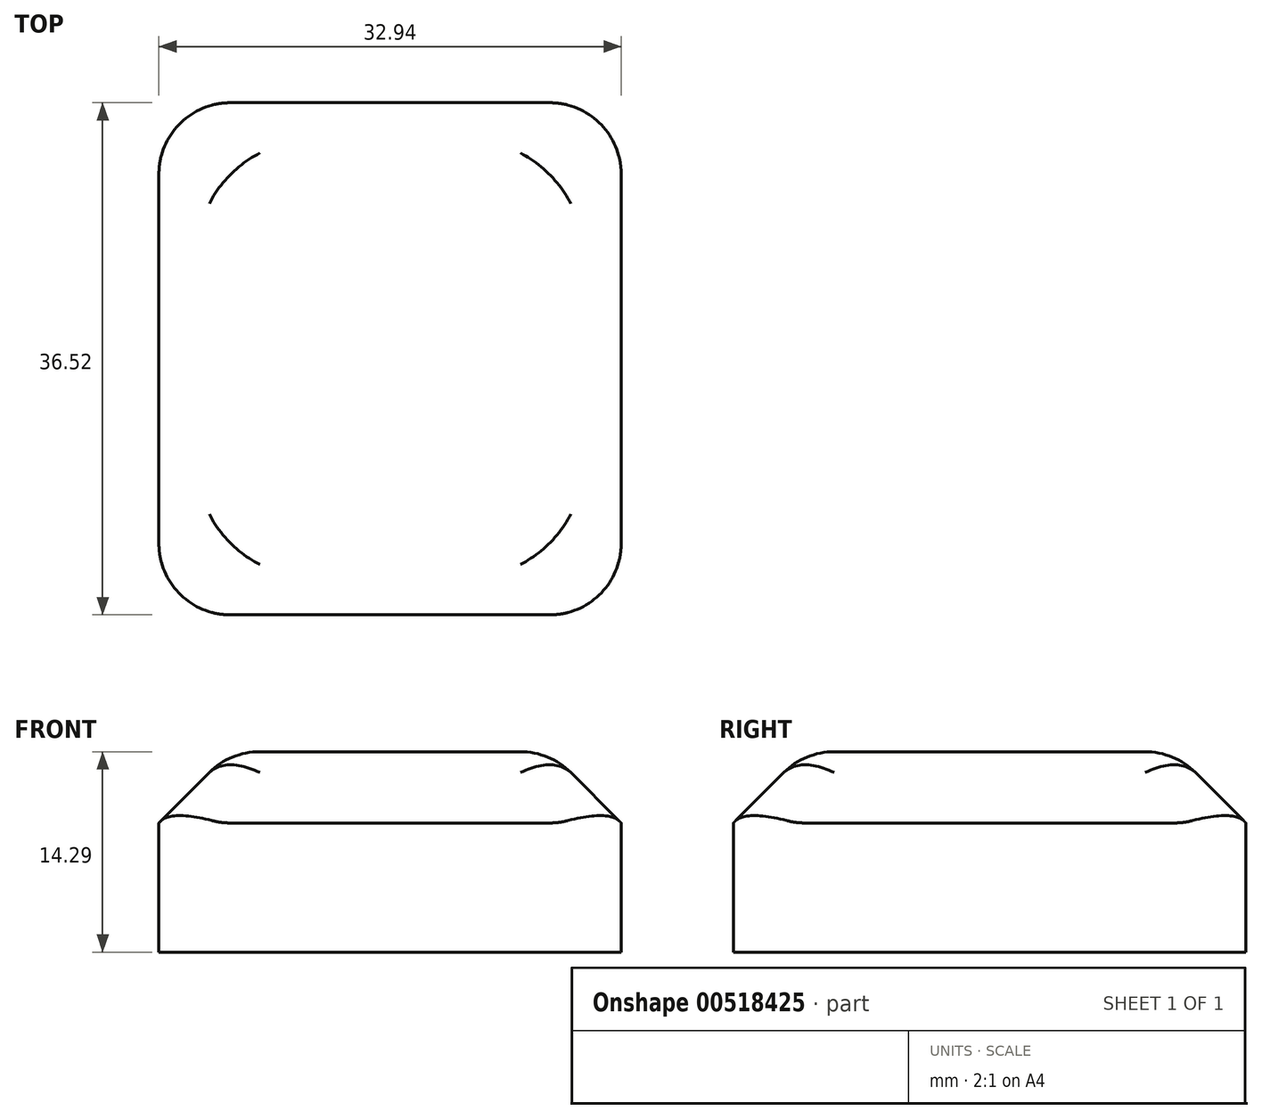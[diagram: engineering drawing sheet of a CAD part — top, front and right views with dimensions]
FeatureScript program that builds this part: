
annotation { "Feature Type Name" : "Feature", "Feature Type Description" : "" }
export const myFeature = defineFeature(function(context is Context, id is Id, definition is map)
    precondition{}
    {
        {
            var Q0;
            Q0=qCreatedBy(makeId("Top.planeOp"),FACE);
            var sketch = newSketch(context, id + "F0", { "sketchPlane" : qUnion([Q0])});
            skLineSegment(sketch, "E0.bottom", {"start": v(16.47, -18.26) * mm, "end": v(-16.47, -18.26) * mm});
            skLineSegment(sketch, "E0.top", {"start": v(16.47, 18.26) * mm, "end": v(-16.47, 18.26) * mm});
            skLineSegment(sketch, "E0.left", {"start": v(16.47, -18.26) * mm, "end": v(16.47, 18.26) * mm});
            skLineSegment(sketch, "E0.right", {"start": v(-16.47, -18.26) * mm, "end": v(-16.47, 18.26) * mm});
            skPoint(sketch, "E0.middle", {"position": v(0, 0) * mm});
            skSolve(sketch);
        }
        {
            var Q0;
            Q0 = qSketchRegion(id + "F0", true);
            extrude(context, id + "F1", {"entities" : qUnion([Q0]), "depth" : 14.29 * mm, "offsetDistance" : 25.4 * mm});
        }
        {
            var Q0;
            Q0=makeQuery(id+"F1.opExtrude","CAP_FACE",FACE,{"disambiguationData":[OSD([sQuery(id+"F0.wireOp",EDGE,"E0.bottom"),sQuery(id+"F0.wireOp",EDGE,"E0.top"),sQuery(id+"F0.wireOp",EDGE,"E0.left"),sQuery(id+"F0.wireOp",EDGE,"E0.right")])],"isStart":false});
            chamfer(context, id + "F2", {"entities" : qUnion([Q0]), "width" : 5.08 * mm, "tangentPropagation" : true});
        }
        {
            var Q0;
            Q0=makeQuery(id+"F1.opExtrude","SWEPT_EDGE",EDGE,{"disambiguationData":[OSD([sQuery(id+"F0.wireOp",EDGE,"E0.bottom"),sQuery(id+"F0.wireOp",EDGE,"E0.left")])]});
            var Q1;
            Q1=makeQuery(id+"F1.opExtrude","SWEPT_EDGE",EDGE,{"disambiguationData":[OSD([sQuery(id+"F0.wireOp",EDGE,"E0.top"),sQuery(id+"F0.wireOp",EDGE,"E0.left")])]});
            var Q2;
            Q2=makeQuery(id+"F1.opExtrude","SWEPT_EDGE",EDGE,{"disambiguationData":[OSD([sQuery(id+"F0.wireOp",EDGE,"E0.top"),sQuery(id+"F0.wireOp",EDGE,"E0.right")])]});
            var Q3;
            Q3=makeQuery(id+"F1.opExtrude","SWEPT_EDGE",EDGE,{"disambiguationData":[OSD([sQuery(id+"F0.wireOp",EDGE,"E0.bottom"),sQuery(id+"F0.wireOp",EDGE,"E0.right")])]});
            var Q4;
            Q4=makeQuery(id+"F1.opExtrude","CAP_FACE",FACE,{"disambiguationData":[OSD([sQuery(id+"F0.wireOp",EDGE,"E0.bottom"),sQuery(id+"F0.wireOp",EDGE,"E0.top"),sQuery(id+"F0.wireOp",EDGE,"E0.left"),sQuery(id+"F0.wireOp",EDGE,"E0.right")])],"isStart":false});
            var Q5;
            Q5=makeQuery(id+"F2.opChamfer","BLEND_EDGE",EDGE,{"blendedFrom":[makeQuery(id+"F1.opExtrude","CAP_EDGE",EDGE,{"disambiguationData":[OSD([sQuery(id+"F0.wireOp",EDGE,"E0.bottom")])],"isStart":false}),makeQuery(id+"F1.opExtrude","CAP_EDGE",EDGE,{"disambiguationData":[OSD([sQuery(id+"F0.wireOp",EDGE,"E0.right")])],"isStart":false})],"blendedInto":[]});
            var Q6;
            Q6=makeQuery(id+"F2.opChamfer","BLEND_EDGE",EDGE,{"blendedFrom":[makeQuery(id+"F1.opExtrude","CAP_EDGE",EDGE,{"disambiguationData":[OSD([sQuery(id+"F0.wireOp",EDGE,"E0.bottom")])],"isStart":false}),makeQuery(id+"F1.opExtrude","CAP_EDGE",EDGE,{"disambiguationData":[OSD([sQuery(id+"F0.wireOp",EDGE,"E0.left")])],"isStart":false})],"blendedInto":[]});
            var Q7;
            Q7=makeQuery(id+"F2.opChamfer","BLEND_EDGE",EDGE,{"blendedFrom":[makeQuery(id+"F1.opExtrude","CAP_EDGE",EDGE,{"disambiguationData":[OSD([sQuery(id+"F0.wireOp",EDGE,"E0.top")])],"isStart":false}),makeQuery(id+"F1.opExtrude","CAP_EDGE",EDGE,{"disambiguationData":[OSD([sQuery(id+"F0.wireOp",EDGE,"E0.left")])],"isStart":false})],"blendedInto":[]});
            var Q8;
            Q8=makeQuery(id+"F2.opChamfer","BLEND_EDGE",EDGE,{"blendedFrom":[makeQuery(id+"F1.opExtrude","CAP_EDGE",EDGE,{"disambiguationData":[OSD([sQuery(id+"F0.wireOp",EDGE,"E0.top")])],"isStart":false}),makeQuery(id+"F1.opExtrude","CAP_EDGE",EDGE,{"disambiguationData":[OSD([sQuery(id+"F0.wireOp",EDGE,"E0.right")])],"isStart":false})],"blendedInto":[]});
            fillet(context, id + "F3", {"entities" : qUnion([Q0, Q1, Q2, Q3, Q4, Q5, Q6, Q7, Q8]), "radius" : 5.08 * mm, "tangentPropagation" : true, "allowEdgeOverflow" : false});
        }
    });
